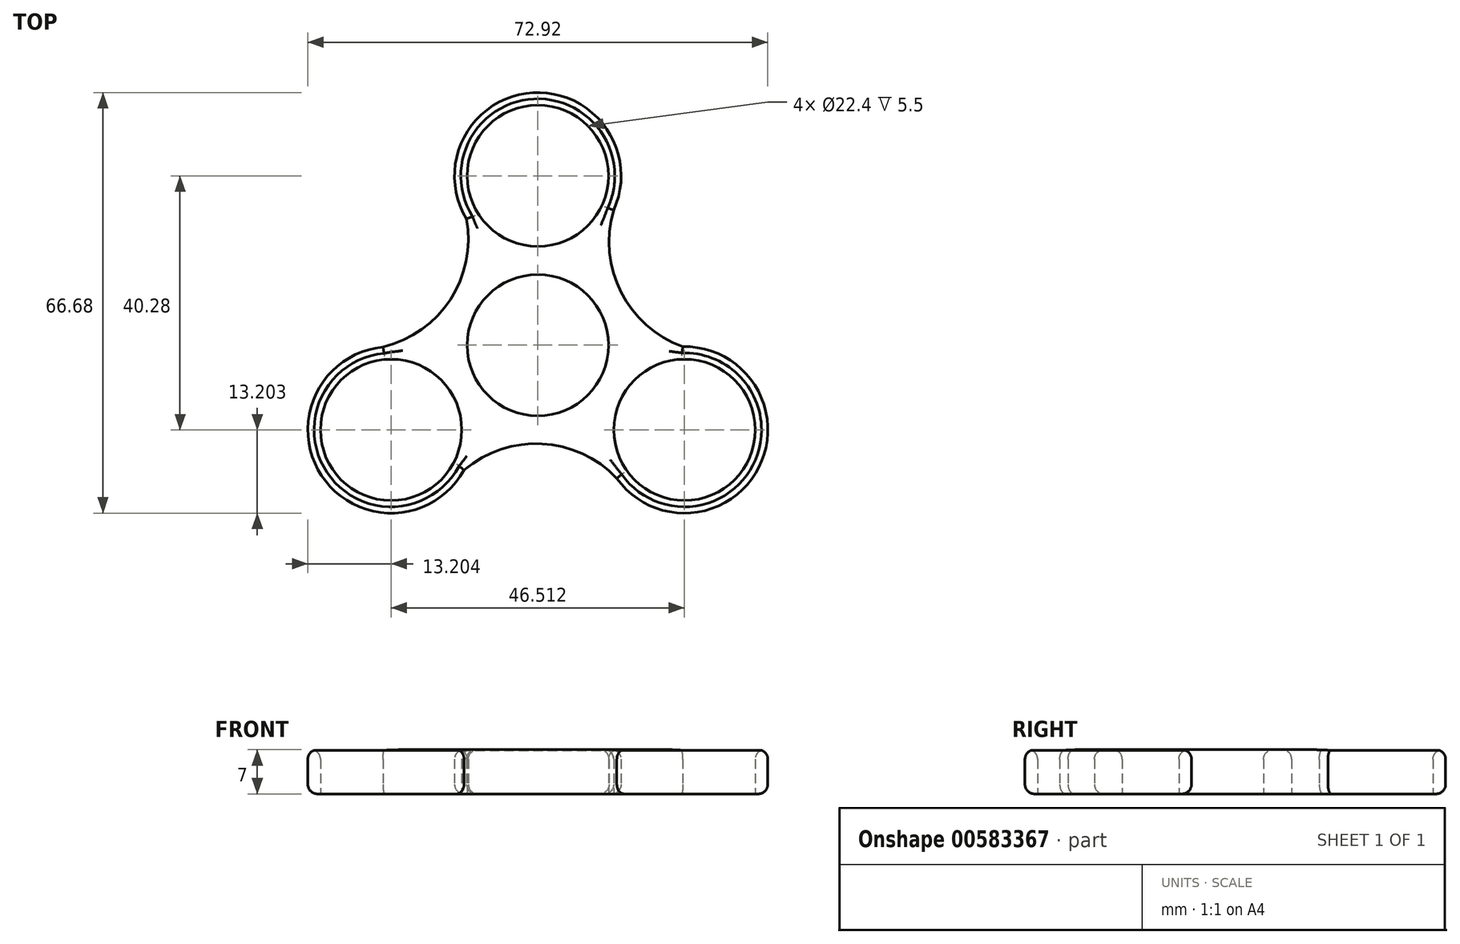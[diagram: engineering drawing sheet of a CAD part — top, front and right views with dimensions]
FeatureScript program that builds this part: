
annotation { "Feature Type Name" : "Feature", "Feature Type Description" : "" }
export const myFeature = defineFeature(function(context is Context, id is Id, definition is map)
    precondition{}
    {
        {
            var Q0;
            Q0=qCreatedBy(makeId("Top.planeOp"),FACE);
            var sketch = newSketch(context, id + "F0", { "sketchPlane" : qUnion([Q0])});
            skCircle(sketch, "E0", {"center": v(0, 0) * mm, "radius": 11.2 * mm});
            skArc(sketch, "E1", {"start": v(12.02, 21.4) * mm, "mid": v(-0.78, 40.03) * mm, "end": v(-11.3, 20.03) * mm});
            skCircle(sketch, "E2", {"center": v(0, 26.85) * mm, "radius": 11.2 * mm});
            skCircle(sketch, "E3.1.0", {"center": v(-23.26, -13.43) * mm, "radius": 11.2 * mm});
            skArc(sketch, "E3.1.1", {"start": v(-24.54, -0.29) * mm, "mid": v(-34.28, -20.69) * mm, "end": v(-11.7, -19.8) * mm});
            skCircle(sketch, "E3.2.0", {"center": v(23.26, -13.43) * mm, "radius": 11.2 * mm});
            skArc(sketch, "E3.2.1", {"start": v(12.52, -21.11) * mm, "mid": v(35.06, -19.34) * mm, "end": v(23, -0.23) * mm});
            skArc(sketch, "E4", {"start": v(12.02, 21.4) * mm, "mid": v(13.2, 8.4) * mm, "end": v(23, -0.23) * mm});
            skArc(sketch, "E5.1.0", {"start": v(-24.54, -0.29) * mm, "mid": v(-13.88, 7.23) * mm, "end": v(-11.3, 20.03) * mm});
            skArc(sketch, "E5.2.0", {"start": v(12.52, -21.11) * mm, "mid": v(0.67, -15.64) * mm, "end": v(-11.7, -19.8) * mm});
            skSolve(sketch);
        }
        {
            var Q0;
            Q0=makeQuery(id+"F0.imprint","IMPRINT",FACE,{"disambiguationData":[TD([[makeQuery(id+"F0.imprint","IMPRINT",EDGE,{"derivedFrom":sQuery(id+"F0.wireOp",EDGE,"E0")}),-1.0]])]});
            extrude(context, id + "F1", {"entities" : qUnion([Q0]), "depth" : 7 * mm, "offsetDistance" : 25 * mm});
        }
        {
            var Q0;
            Q0=makeQuery(id+"F1.opExtrude","CAP_EDGE",EDGE,{"disambiguationData":[OSD([sQuery(id+"F0.wireOp",EDGE,"E5.2.0")])],"isStart":false});
            var Q1;
            Q1=makeQuery(id+"F1.opExtrude","CAP_EDGE",EDGE,{"disambiguationData":[OSD([sQuery(id+"F0.wireOp",EDGE,"E3.1.1")])],"isStart":false});
            var Q2;
            Q2=makeQuery(id+"F1.opExtrude","CAP_FACE",FACE,{"disambiguationData":[OSD([sQuery(id+"F0.wireOp",EDGE,"E0"),sQuery(id+"F0.wireOp",EDGE,"E1"),sQuery(id+"F0.wireOp",EDGE,"E2"),sQuery(id+"F0.wireOp",EDGE,"E3.1.0"),sQuery(id+"F0.wireOp",EDGE,"E3.1.1"),sQuery(id+"F0.wireOp",EDGE,"E3.2.0"),sQuery(id+"F0.wireOp",EDGE,"E3.2.1"),sQuery(id+"F0.wireOp",EDGE,"E4"),sQuery(id+"F0.wireOp",EDGE,"E5.1.0"),sQuery(id+"F0.wireOp",EDGE,"E5.2.0")])],"isStart":false});
            var Q3;
            Q3=makeQuery(id+"F1.opExtrude","CAP_EDGE",EDGE,{"disambiguationData":[OSD([sQuery(id+"F0.wireOp",EDGE,"E3.2.0")])],"isStart":false});
            fillet(context, id + "F2", {"entities" : qUnion([Q0, Q1, Q2, Q3]), "radius" : 1.5 * mm, "tangentPropagation" : true, "allowEdgeOverflow" : false});
        }
        {
            var Q0;
            Q0=makeQuery(id+"F1.opExtrude","CAP_EDGE",EDGE,{"disambiguationData":[OSD([sQuery(id+"F0.wireOp",EDGE,"E3.2.1")])],"isStart":true});
            var Q1;
            Q1=makeQuery(id+"F1.opExtrude","CAP_EDGE",EDGE,{"disambiguationData":[OSD([sQuery(id+"F0.wireOp",EDGE,"E4")])],"isStart":true});
            var Q2;
            Q2=makeQuery(id+"F1.opExtrude","CAP_EDGE",EDGE,{"disambiguationData":[OSD([sQuery(id+"F0.wireOp",EDGE,"E1")])],"isStart":true});
            var Q3;
            Q3=makeQuery(id+"F1.opExtrude","CAP_EDGE",EDGE,{"disambiguationData":[OSD([sQuery(id+"F0.wireOp",EDGE,"E5.1.0")])],"isStart":true});
            var Q4;
            Q4=makeQuery(id+"F1.opExtrude","CAP_EDGE",EDGE,{"disambiguationData":[OSD([sQuery(id+"F0.wireOp",EDGE,"E3.1.1")])],"isStart":true});
            var Q5;
            Q5=makeQuery(id+"F1.opExtrude","CAP_EDGE",EDGE,{"disambiguationData":[OSD([sQuery(id+"F0.wireOp",EDGE,"E5.2.0")])],"isStart":true});
            fillet(context, id + "F3", {"entities" : qUnion([Q0, Q1, Q2, Q3, Q4, Q5]), "radius" : 1.5 * mm, "tangentPropagation" : true, "allowEdgeOverflow" : false});
        }
    });
